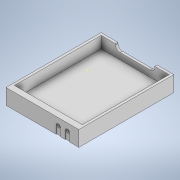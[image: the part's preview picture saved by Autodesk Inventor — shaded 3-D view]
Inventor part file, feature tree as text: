
AUTODESK INVENTOR PART (.ipt)
format: ipt  version: 2021.2 (Build 252289000, 289)  size: 522,240 bytes
history: native  units: in
note: dims shown in document units (in); Inventor stores cm internally (conversion verified against a paired STEP export)
features: sketch x34, extrude x30, fillet x1
ambient origin geometry x8: Origin, YZ Plane, XZ Plane, XY Plane, X Axis, Y Axis, Z Axis, Center Point
bodies: Solid1 (feature_tree)
feature tree (65):
  extrude  "Extrusion1"  Depth=1.315in
  extrude  "Extrusion2"  Depth=0.0433in
  extrude  "Extrusion3"  Depth=0.0433in
  extrude  "Extrusion4"  Depth=1.5669in
  sketch  "Sketch6"  dims[d11=0.1929in d12=0.0in d13=0.0236in d14=0.0in]
  extrude  "Extrusion5"  Depth=0.0236in TaperAngle=0.0deg
  extrude  "Extrusion6"  Depth=0.1181in
  sketch  "Sketch8"  dims[d18=0.0512in d19=0.1417in]
  extrude  "Extrusion7"  Depth=0.1417in
  extrude  "Extrusion8"  Depth=0.0984in TaperAngle=0.0deg
  extrude  "Extrusion9"  Depth=0.0394in
  extrude  "Extrusion10"  Depth=0.0394in
  extrude  "Extrusion11"  TaperAngle=0.0deg  [1 undecoded]
  sketch  "Sketch14"  dims[d35=0.0118in d36=0.0512in d37=0.0in]
  extrude  "Extrusion12"  Depth=0.0787in
  extrude  "Extrusion13"  TaperAngle=0.0deg  [1 undecoded]
  extrude  "Extrusion14"  Depth=0.0118in
  extrude  "Extrusion15"  Depth=0.0787in
  extrude  "Extrusion16"  Depth=0.0984in
  sketch  "Sketch20"  dims[d51=0.0512in d52=0.0394in d53=0.0591in d54=0.0591in]
  extrude  "Extrusion17"  TaperAngle=0.0deg  [1 undecoded]
  sketch  "Sketch22"  dims[d57=0.0591in d58=0.0in d59=0.0315in]
  extrude  "Extrusion18"  Depth=0.0394in
  extrude  "Extrusion19"  Depth=0.0394in
  extrude  "Extrusion20"  TaperAngle=0.0deg  [1 undecoded]
  extrude  "Extrusion21"  Depth=0.0315in
  extrude  "Extrusion22"  Depth=0.0433in
  extrude  "Extrusion23"  TaperAngle=0.0deg  [1 undecoded]
  sketch  "Sketch29"  dims[d80=0.0787in d81=0.0in d82=0.0394in]
  extrude  "Extrusion24"  Depth=0.0433in TaperAngle=0.0deg
  extrude  "Extrusion25"  TaperAngle=0.0deg  [1 undecoded]
  extrude  "Extrusion26"  Depth=0.0079in
  extrude  "Extrusion27"  Depth=0.0433in TaperAngle=0.0deg
  extrude  "Extrusion28"  Depth=0.0394in
  extrude  "Extrusion29"  Depth=0.0787in
  fillet  "Fillet1"  Radius=0.0394in
  extrude  "Extrusion30"  Depth=0.0984in TaperAngle=0.0deg
  sketch  "Sketch2"  dims[d2=1.6535in d3=1.315in]
  sketch  "Sketch3"  dims[d4=0.2362in d5=0.0in d6=0.0433in]
  sketch  "Sketch4"  dims[d7=0.0433in d8=0.0433in]
  sketch  "Sketch5"  dims[d9=0.0433in d10=1.5669in]
  sketch  "Sketch7"  dims[d15=0.1181in d16=0.0in d17=0.1181in]
  sketch  "Sketch9"  dims[d20=0.0394in d21=0.0984in d22=0.0in]
  sketch  "Sketch10"  dims[d23=0.1181in d24=0.0512in d25=0.1181in d26=0.0512in d27=0.0394in]
  sketch  "Sketch11"  dims[d28=0.0394in d29=0.0276in]
  sketch  "Sketch12"  dims[d30=0.0276in d31=0.0in d32=0.0in]
  sketch  "Sketch13"  dims[d33=0.0118in d34=0.0787in]
  sketch  "Sketch15"  dims[d38=0.0792in d39=0.0118in d40=0.0512in]
  sketch  "Sketch16"  dims[d41=0.0in d42=0.0787in]
  sketch  "Sketch17"  dims[d43=0.0984in d44=0.0in d45=0.0512in]
  sketch  "Sketch18"  dims[d46=0.0394in d47=0.0in]
  sketch  "Sketch19"  dims[d48=0.0591in d49=0.0512in d50=0.0394in]
  sketch  "Sketch21"  dims[d55=0.0in d56=0.0in]
  sketch  "Sketch23"  dims[d60=0.0591in d61=0.0in d62=0.0433in]
  sketch  "Sketch24"  dims[d63=0.0in d64=0.0in d65=0.0in d66=0.0in]
  sketch  "Sketch25"  dims[d67=0.0433in d68=0.0in d69=0.0433in d70=0.0in]
  sketch  "Sketch26"  dims[d71=0.0433in d72=0.0in d73=0.0in]
  sketch  "Sketch27"  dims[d74=0.0079in d75=0.0079in]
  sketch  "Sketch28"  dims[d76=0.0433in d77=0.0in d78=0.0433in d79=0.0in]
  sketch  "Sketch30"  dims[d83=0.0787in d84=0.0787in d85=0.0394in]
  sketch  "Sketch31"  dims[d86=0.0295in d87=0.0984in d88=0.0in]
  sketch  "Sketch32"  dims[d89=0.0295in]
  sketch  "Sketch33"  dims[d90=0.0787in]
  sketch  "Sketch34"  dims[d91=0.0394in]
  sketch  "Sketch35"  dims[d92=0.0295in d93=0.0394in d94=0.0787in d95=0.0039in d96=0.0in d97=0.0984in d98=0.0in d99=0.0591in d100=0.0591in d101=0.0984in d102=0.0in d103=0.0039in d104=0.0in d105=0.0079in d106=0.0in d107=0.0079in d108=0.0in d109=0.0079in d110=0.0in d111=0.1181in d112=0.0in d113=0.0394in d114=0.0in d115=0.0197in d116=0.0in d117=0.7087in d118=0.3031in d119=0.0984in d120=0.0472in d121=0.0in d122=0.0787in d123=0.0118in d124=0.0in]
note: 6 required parameter values undecoded (feature->parameter linkage not recoverable at this tier; creation-order binding heuristic only, values carry confidence <= 0.55)
